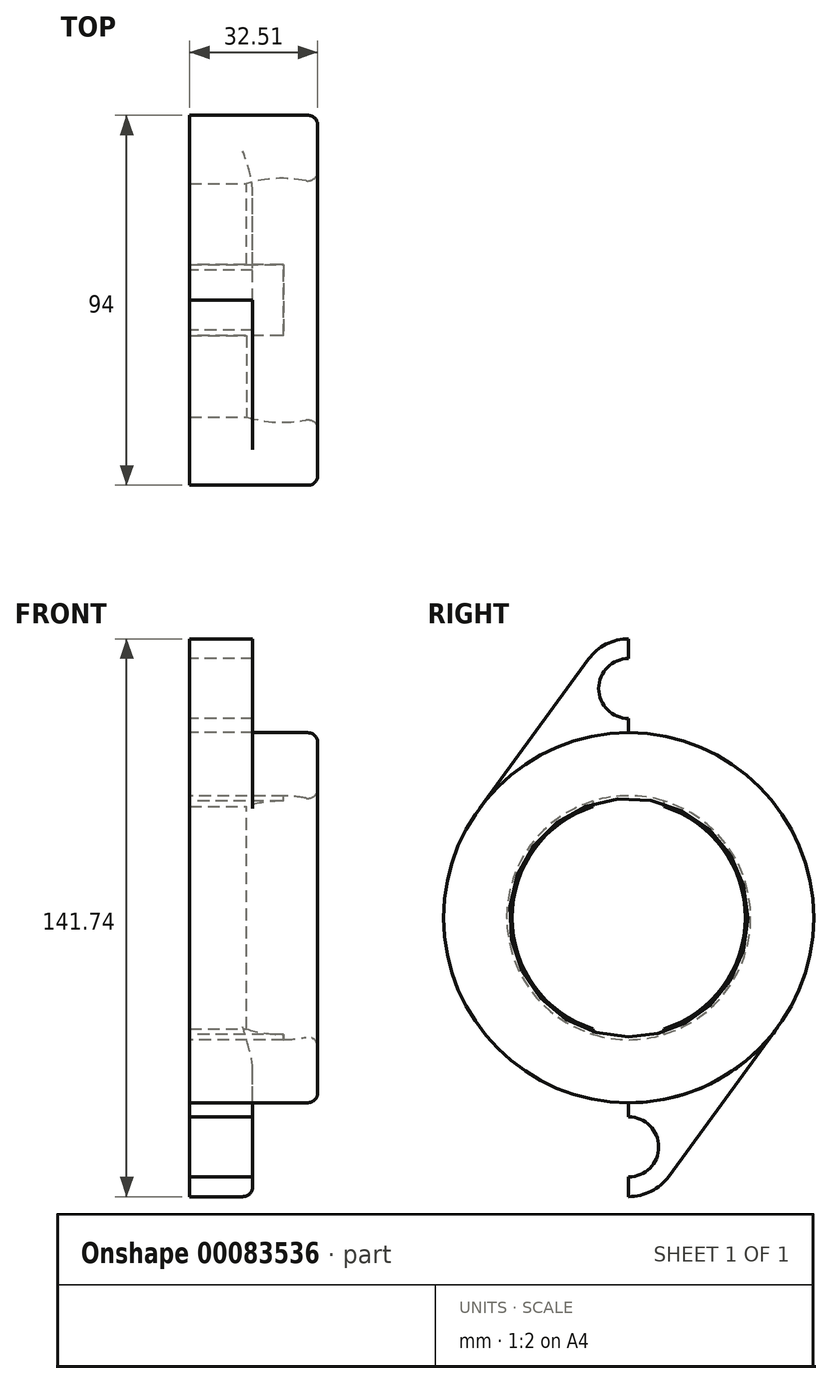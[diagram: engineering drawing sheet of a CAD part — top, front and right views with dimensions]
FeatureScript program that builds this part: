
annotation { "Feature Type Name" : "Feature", "Feature Type Description" : "" }
export const myFeature = defineFeature(function(context is Context, id is Id, definition is map)
    precondition{}
    {
        {
            var Q0;
            Q0=qCreatedBy(makeId("Right.planeOp"),FACE);
            var sketch = newSketch(context, id + "F0", { "sketchPlane" : qUnion([Q0])});
            skCircle(sketch, "E0", {"center": v(0, 0) * mm, "radius": 47 * mm});
            skLineSegment(sketch, "E1", {"start": v(0, 0) * mm, "end": v(-9.26, 0) * mm});
            skLineSegment(sketch, "E2", {"start": v(0, 0) * mm, "end": v(0, 58.24) * mm});
            skLineSegment(sketch, "E3", {"start": v(0, 0) * mm, "end": v(0, 70.87) * mm});
            skArc(sketch, "E4", {"start": v(0, 70.87) * mm, "mid": v(-5.71, 69.5) * mm, "end": v(-10.19, 65.7) * mm});
            skCircle(sketch, "E5", {"center": v(0, 58.24) * mm, "radius": 7.62 * mm});
            skLineSegment(sketch, "E6", {"start": v(-10.19, 65.7) * mm, "end": v(-37.94, 27.74) * mm});
            skArc(sketch, "E7.MirrorCS", {"start": v(0, 70.87) * mm, "mid": v(5.71, 69.5) * mm, "end": v(10.19, 65.7) * mm});
            skLineSegment(sketch, "E8.MirrorCS", {"start": v(10.19, 65.7) * mm, "end": v(37.94, 27.74) * mm});
            skLineSegment(sketch, "E9.MirrorCS", {"start": v(0, 0) * mm, "end": v(0, -58.24) * mm});
            skLineSegment(sketch, "E10.MirrorCS", {"start": v(10.19, -65.7) * mm, "end": v(37.94, -27.74) * mm});
            skLineSegment(sketch, "E11.MirrorCS", {"start": v(0, 0) * mm, "end": v(0, -70.87) * mm});
            skArc(sketch, "E12.MirrorCS", {"start": v(0, -70.87) * mm, "mid": v(-5.71, -69.5) * mm, "end": v(-10.19, -65.7) * mm});
            skArc(sketch, "E13.MirrorCS", {"start": v(0, -70.87) * mm, "mid": v(5.71, -69.5) * mm, "end": v(10.19, -65.7) * mm});
            skLineSegment(sketch, "E14.MirrorCS", {"start": v(-10.19, -65.7) * mm, "end": v(-37.94, -27.74) * mm});
            skCircle(sketch, "E15.MirrorC", {"center": v(0, -58.24) * mm, "radius": 7.62 * mm});
            skSolve(sketch);
        }
        {
            var Q0;
            {var subQ0=sQuery(id+"F0.wireOp",EDGE,"E4");Q0=makeQuery(id+"F0.imprint","IMPRINT",FACE,{"disambiguationData":[TD([[makeQuery(id+"F0.imprint","IMPRINT",EDGE,{"derivedFrom":subQ0}),1.0]])]});}
            var Q1;
            {var subQ4=sQuery(id+"F0.wireOp",EDGE,"E7.MirrorCS");Q1=makeQuery(id+"F0.imprint","IMPRINT",FACE,{"disambiguationData":[TD([[makeQuery(id+"F0.imprint","IMPRINT",EDGE,{"derivedFrom":subQ4}),-1.0]])]});}
            var Q2;
            {var subQ0=sQuery(id+"F0.wireOp",EDGE,"E10.MirrorCS");Q2=makeQuery(id+"F0.imprint","IMPRINT",FACE,{"disambiguationData":[TD([[makeQuery(id+"F0.imprint","IMPRINT",EDGE,{"derivedFrom":subQ0}),1.0]])]});}
            var Q3;
            {var subQ0=sQuery(id+"F0.wireOp",EDGE,"E12.MirrorCS");Q3=makeQuery(id+"F0.imprint","IMPRINT",FACE,{"disambiguationData":[TD([[makeQuery(id+"F0.imprint","IMPRINT",EDGE,{"derivedFrom":subQ0}),-1.0]])]});}
            extrude(context, id + "F1", {"entities" : qUnion([Q0, Q1, Q2, Q3]), "depth" : 16 * mm});
        }
        {
            var Q0;
            {var subQ3=sQuery(id+"F0.wireOp",EDGE,"E0");var subQ7=makeQuery(id+"F0.imprint","INTERSECT",VERTEX,{"derivedFrom":[subQ3,sQuery(id+"F0.wireOp",EDGE,"E6")]});Q0=makeQuery(id+"F0.imprint","IMPRINT",FACE,{"disambiguationData":[TD([[makeQuery(id+"F0.imprint","IMPRINT",EDGE,{"disambiguationData":[TD([[subQ7,1.0]])],"derivedFrom":subQ3}),1.0]])]});}
            var Q1;
            {var subQ3=sQuery(id+"F0.wireOp",EDGE,"E0");var subQ5=makeQuery(id+"F0.imprint","INTERSECT",VERTEX,{"derivedFrom":[subQ3,sQuery(id+"F0.wireOp",EDGE,"E8.MirrorCS")]});Q1=makeQuery(id+"F0.imprint","IMPRINT",FACE,{"disambiguationData":[TD([[makeQuery(id+"F0.imprint","IMPRINT",EDGE,{"disambiguationData":[TD([[subQ5,-1.0]])],"derivedFrom":subQ3}),1.0]])]});}
            extrude(context, id + "F2", {"entities" : qUnion([Q0, Q1]), "operationType" : NewBodyOperationType.ADD, "depth" : 32.5 * mm});
        }
        {
            var Q0;
            Q0=qCreatedBy(makeId("Front.planeOp"),FACE);
            var sketch = newSketch(context, id + "F3", { "sketchPlane" : qUnion([Q0])});
            skLineSegment(sketch, "E16", {"start": v(0, 0) * mm, "end": v(14.38, 0) * mm});
            skLineSegment(sketch, "E17", {"start": v(14.38, 0) * mm, "end": v(32.38, 0) * mm});
            skLineSegment(sketch, "E18", {"start": v(23.38, 0) * mm, "end": v(23.38, 30.99) * mm});
            skArc(sketch, "E19", {"start": v(23.38, 30.99) * mm, "mid": v(45.3, 21.91) * mm, "end": v(54.37, 0) * mm});
            skArc(sketch, "E20", {"start": v(23.38, 30.99) * mm, "mid": v(18.83, 30.65) * mm, "end": v(14.38, 29.65) * mm});
            skLineSegment(sketch, "E21", {"start": v(14.38, 29.65) * mm, "end": v(-4.9, 29.65) * mm});
            skLineSegment(sketch, "E22", {"start": v(-4.9, 29.65) * mm, "end": v(0, 0) * mm});
            skLineSegment(sketch, "E23", {"start": v(54.37, 0) * mm, "end": v(32.38, 0) * mm});
            skPoint(sketch, "E24.trimOffspring.end.orphan", {"position": v(-7.6, 0) * mm});
            skSolve(sketch);
        }
        {
            var Q0;
            {var subQ2=sQuery(id+"F3.wireOp",EDGE,"E18");Q0=makeQuery(id+"F3.imprint","IMPRINT",FACE,{"disambiguationData":[TD([[makeQuery(id+"F3.imprint","IMPRINT",EDGE,{"derivedFrom":subQ2}),-1.0]])]});}
            var Q1;
            {var subQ1=sQuery(id+"F3.wireOp",EDGE,"E16");Q1=makeQuery(id+"F3.imprint","IMPRINT",FACE,{"disambiguationData":[TD([[makeQuery(id+"F3.imprint","IMPRINT",EDGE,{"derivedFrom":subQ1}),1.0]])]});}
            var Q2;
            Q2=sQuery(id+"F3.wireOp",EDGE,"E17");
            revolve(context, id + "F4", {"operationType" : NewBodyOperationType.REMOVE, "entities" : qUnion([Q0, Q1]), "axis" : qUnion([Q2]), "revolveType" : RevolveType.FULL, "oppositeDirection" : true});
        }
        {
            var Q0;
            Q0=qCreatedBy(makeId("Right.planeOp"),FACE);
            var sketch = newSketch(context, id + "F5", { "sketchPlane" : qUnion([Q0])});
            skLineSegment(sketch, "E25", {"start": v(0, 0) * mm, "end": v(0, 30.99) * mm});
            skArc(sketch, "E26", {"start": v(9.02, 29.65) * mm, "mid": v(0, 30.99) * mm, "end": v(-9.02, 29.65) * mm});
            skLineSegment(sketch, "E27", {"start": v(0, 0) * mm, "end": v(9.02, 0) * mm});
            skLineSegment(sketch, "E28", {"start": v(0, 0) * mm, "end": v(-9.02, 0) * mm});
            skLineSegment(sketch, "E29", {"start": v(-9.02, 0) * mm, "end": v(-9.02, 29.65) * mm});
            skLineSegment(sketch, "E30", {"start": v(9.02, 0) * mm, "end": v(9.02, 29.65) * mm});
            skLineSegment(sketch, "E31.MirrorCS", {"start": v(9.02, 0) * mm, "end": v(9.02, -29.65) * mm});
            skArc(sketch, "E32.MirrorCS", {"start": v(9.02, -29.65) * mm, "mid": v(0, -30.99) * mm, "end": v(-9.02, -29.65) * mm});
            skLineSegment(sketch, "E33.MirrorCS", {"start": v(-9.02, 0) * mm, "end": v(-9.02, -29.65) * mm});
            skSolve(sketch);
        }
        {
            var Q0;
            Q0 = qSketchRegion(id + "F5", true);
            extrude(context, id + "F6", {"entities" : qUnion([Q0]), "operationType" : NewBodyOperationType.REMOVE, "depth" : 23.8 * mm});
        }
        {
            var Q0;
            Q0=makeQuery(id+"F2.opExtrude","CAP_EDGE",EDGE,{"disambiguationData":[OSD([sQuery(id+"F0.wireOp",EDGE,"E0")])],"isStart":false});
            var Q1;
            Q1=makeQuery(id+"F1.opExtrude","CAP_EDGE",EDGE,{"disambiguationData":[OSD([sQuery(id+"F0.wireOp",EDGE,"E8.MirrorCS")])],"isStart":false});
            var Q2;
            Q2=makeQuery(id+"F1.opExtrude","CAP_EDGE",EDGE,{"disambiguationData":[OSD([sQuery(id+"F0.wireOp",EDGE,"E10.MirrorCS")])],"isStart":false});
            var Q3;
            Q3=makeQuery(id+"F4.boolean.opBoolean","INTERSECT",EDGE,{"derivedFrom":[makeQuery(id+"F2.opExtrude","CAP_FACE",FACE,{"disambiguationData":[OSD([sQuery(id+"F0.wireOp",EDGE,"E0")])],"isStart":false}),makeQuery(id+"F4.opRevolve","SWEPT_FACE",FACE,{"disambiguationData":[OSD([sQuery(id+"F3.wireOp",EDGE,"E19"),sQuery(id+"F3.wireOp",EDGE,"E20")])]})]});
            var Q4;
            {var subQ0=sQuery(id+"F0.wireOp",EDGE,"E0");Q4=makeQuery(id+"F1.opExtrude","CAP_EDGE",EDGE,{"disambiguationData":[OSD([subQ0]),TDD([makeQuery(id+"F0.imprint","IMPRINT",EDGE,{"disambiguationData":[TD([[makeQuery(id+"F0.imprint","INTERSECT",VERTEX,{"derivedFrom":[subQ0,sQuery(id+"F0.wireOp",EDGE,"E8.MirrorCS")]}),-1.0]])],"derivedFrom":subQ0}),makeQuery(id+"F0.imprint","IMPRINT",EDGE,{"disambiguationData":[TD([[makeQuery(id+"F0.imprint","INTERSECT",VERTEX,{"derivedFrom":[subQ0,sQuery(id+"F0.wireOp",EDGE,"E6")]}),1.0]])],"derivedFrom":subQ0})])],"isStart":false});}
            var Q5;
            {var subQ0=sQuery(id+"F0.wireOp",EDGE,"E0");Q5=makeQuery(id+"F1.opExtrude","CAP_EDGE",EDGE,{"disambiguationData":[OSD([subQ0]),TDD([makeQuery(id+"F0.imprint","IMPRINT",EDGE,{"disambiguationData":[TD([[makeQuery(id+"F0.imprint","INTERSECT",VERTEX,{"derivedFrom":[subQ0,sQuery(id+"F0.wireOp",EDGE,"E14.MirrorCS")]}),-1.0]])],"derivedFrom":subQ0}),makeQuery(id+"F0.imprint","IMPRINT",EDGE,{"disambiguationData":[TD([[makeQuery(id+"F0.imprint","INTERSECT",VERTEX,{"derivedFrom":[subQ0,sQuery(id+"F0.wireOp",EDGE,"E10.MirrorCS")]}),1.0]])],"derivedFrom":subQ0})])],"isStart":false});}
            fillet(context, id + "F7", {"entities" : qUnion([Q0, Q1, Q2, Q3, Q4, Q5]), "radius" : 2.54 * mm, "tangentPropagation" : true, "allowEdgeOverflow" : false});
        }
    });
